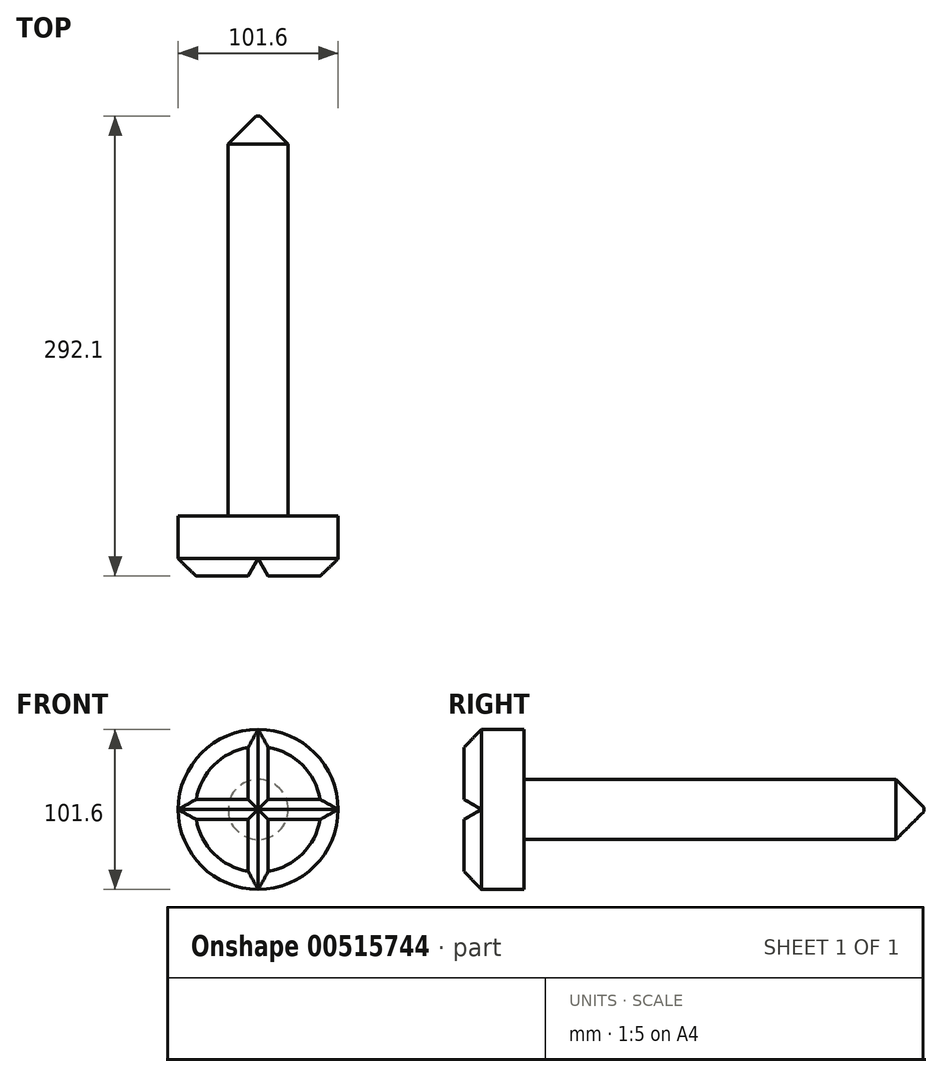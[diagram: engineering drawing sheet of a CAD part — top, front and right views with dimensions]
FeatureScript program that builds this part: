
annotation { "Feature Type Name" : "Feature", "Feature Type Description" : "" }
export const myFeature = defineFeature(function(context is Context, id is Id, definition is map)
    precondition{}
    {
        {
            var Q0;
            Q0=qCreatedBy(makeId("Front.planeOp"),FACE);
            var sketch = newSketch(context, id + "F0", { "sketchPlane" : qUnion([Q0])});
            skCircle(sketch, "E0", {"center": v(0, 0) * mm, "radius": 19.05 * mm});
            skSolve(sketch);
        }
        {
            var Q0;
            Q0 = qSketchRegion(id + "F0", true);
            extrude(context, id + "F1", {"entities" : qUnion([Q0]), "depth" : 254 * mm, "offsetDistance" : 25.4 * mm});
        }
        {
            var Q0;
            Q0=makeQuery(id+"F1.opExtrude","CAP_FACE",FACE,{"disambiguationData":[OSD([sQuery(id+"F0.wireOp",EDGE,"E0")])],"isStart":false});
            var sketch = newSketch(context, id + "F2", { "sketchPlane" : qUnion([Q0])});
            skCircle(sketch, "E1", {"center": v(0, 0) * mm, "radius": 50.8 * mm});
            skSolve(sketch);
        }
        {
            var Q0;
            Q0 = qSketchRegion(id + "F2", true);
            extrude(context, id + "F3", {"entities" : qUnion([Q0]), "operationType" : NewBodyOperationType.ADD, "depth" : 38.1 * mm, "offsetDistance" : 25.4 * mm});
        }
        {
            var Q0;
            Q0=makeQuery(id+"F3.opExtrude","CAP_FACE",FACE,{"disambiguationData":[OSD([sQuery(id+"F2.wireOp",EDGE,"E1")])],"isStart":false});
            var sketch = newSketch(context, id + "F4", { "sketchPlane" : qUnion([Q0])});
            skLineSegment(sketch, "E2", {"start": v(0, 0) * mm, "end": v(0, -50.8) * mm});
            skLineSegment(sketch, "E3", {"start": v(0, 0) * mm, "end": v(50.8, 0) * mm});
            skLineSegment(sketch, "E4", {"start": v(0, 0) * mm, "end": v(0, 50.8) * mm});
            skLineSegment(sketch, "E5", {"start": v(0, 0) * mm, "end": v(-50.8, 0) * mm});
            skSolve(sketch);
        }
        {
            var Q0;
            Q0=qCreatedBy(makeId("Top.planeOp"),FACE);
            var sketch = newSketch(context, id + "F5", { "sketchPlane" : qUnion([Q0])});
            skLineSegment(sketch, "E6", {"start": v(0, -292.1) * mm, "end": v(0, -281.1) * mm});
            skLineSegment(sketch, "E7", {"start": v(0, -281.1) * mm, "end": v(6.35, -292.1) * mm});
            skLineSegment(sketch, "E8", {"start": v(6.35, -292.1) * mm, "end": v(-6.35, -292.1) * mm});
            skLineSegment(sketch, "E9", {"start": v(-6.35, -292.1) * mm, "end": v(0, -281.1) * mm});
            skSolve(sketch);
        }
        {
            var Q0;
            Q0 = qSketchRegion(id + "F5", true);
            extrude(context, id + "F6", {"entities" : qUnion([Q0]), "operationType" : NewBodyOperationType.REMOVE, "oppositeDirection" : true, "depth" : 50.8 * mm, "offsetDistance" : 25.4 * mm});
        }
        {
            var Q0;
            Q0 = qSketchRegion(id + "F5", true);
            extrude(context, id + "F7", {"entities" : qUnion([Q0]), "operationType" : NewBodyOperationType.REMOVE, "depth" : 50.8 * mm, "offsetDistance" : 25.4 * mm});
        }
        {
            var Q0;
            {var subQ0=sQuery(id+"F2.wireOp",EDGE,"E1");var subQ1=sQuery(id+"F5.wireOp",EDGE,"E9");Q0=makeQuery(id+"F7.boolean.opBoolean","SPLIT",EDGE,{"disambiguationData":[TD([makeQuery(id+"F6.boolean.opBoolean","COPY",FACE,{"derivedFrom":makeQuery(id+"F6.opExtrude","SWEPT_FACE",FACE,{"disambiguationData":[OSD([subQ1])]})})])],"derivedFrom":makeQuery(id+"F3.opExtrude","CAP_EDGE",EDGE,{"disambiguationData":[OSD([subQ0])],"isStart":false})});}
            var Q1;
            {var subQ0=sQuery(id+"F2.wireOp",EDGE,"E1");var subQ1=sQuery(id+"F5.wireOp",EDGE,"E7");Q1=makeQuery(id+"F7.boolean.opBoolean","SPLIT",EDGE,{"disambiguationData":[TD([makeQuery(id+"F6.boolean.opBoolean","COPY",FACE,{"derivedFrom":makeQuery(id+"F6.opExtrude","SWEPT_FACE",FACE,{"disambiguationData":[OSD([subQ1])]})})])],"derivedFrom":makeQuery(id+"F3.opExtrude","CAP_EDGE",EDGE,{"disambiguationData":[OSD([subQ0])],"isStart":false})});}
            chamfer(context, id + "F8", {"entities" : qUnion([Q0, Q1]), "width" : 11 * mm, "tangentPropagation" : true});
        }
        {
            var Q0;
            Q0=makeQuery(id+"F1.opExtrude","CAP_EDGE",EDGE,{"disambiguationData":[OSD([sQuery(id+"F0.wireOp",EDGE,"E0")])],"isStart":true});
            chamfer(context, id + "F9", {"entities" : qUnion([Q0]), "width" : 17.78 * mm, "tangentPropagation" : true});
        }
        {
            var Q0;
            Q0=qCreatedBy(makeId("Right.planeOp"),FACE);
            var sketch = newSketch(context, id + "F10", { "sketchPlane" : qUnion([Q0])});
            skLineSegment(sketch, "E10", {"start": v(-292.1, 0) * mm, "end": v(-281.1, 0) * mm});
            skLineSegment(sketch, "E11", {"start": v(-281.1, 0) * mm, "end": v(-292.1, 6.35) * mm});
            skLineSegment(sketch, "E12", {"start": v(-292.1, 6.35) * mm, "end": v(-292.1, -6.35) * mm});
            skLineSegment(sketch, "E13", {"start": v(-292.1, -6.35) * mm, "end": v(-281.1, 0) * mm});
            skSolve(sketch);
        }
        {
            var Q0;
            Q0 = qSketchRegion(id + "F10", true);
            extrude(context, id + "F11", {"entities" : qUnion([Q0]), "operationType" : NewBodyOperationType.REMOVE, "oppositeDirection" : true, "depth" : 50.8 * mm, "offsetDistance" : 25.4 * mm});
        }
        {
            var Q0;
            Q0 = qSketchRegion(id + "F10", true);
            extrude(context, id + "F12", {"entities" : qUnion([Q0]), "operationType" : NewBodyOperationType.REMOVE, "depth" : 50.8 * mm, "offsetDistance" : 25.4 * mm});
        }
    });
